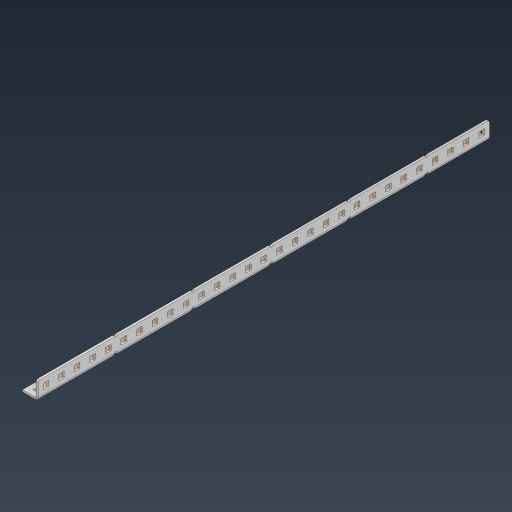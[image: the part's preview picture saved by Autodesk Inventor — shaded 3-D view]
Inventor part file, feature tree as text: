
AUTODESK INVENTOR PART (.ipt)
format: ipt  version: 2024.3 (Build 283343000, 343)  size: 1,099,264 bytes
history: native  units: in
note: dims shown in document units (in); Inventor stores cm internally (conversion verified against a paired STEP export)
features: other x94, extrude x85, sheet_metal_op x11, pattern_linear x2, mirror x1, chamfer x1, sketch x1
ambient origin geometry x8: Origin, YZ Plane, XZ Plane, XY Plane, X Axis, Y Axis, Z Axis, Center Point
bodies: Solid1 (feature_tree), Body (feature_tree)
feature tree (195):
  sheet_metal_op  "Flanges"
  other  "Flange Pattern Plane"
  other  "Flange Pattern Sketch"
  sheet_metal_op  "Flange Pattern"
  sheet_metal_op  "Body Pattern"
  pattern_linear  "Center Pattern"  Spacing1=14.5in  [1 undecoded]
  other  "Arc Length"
  mirror  "Notch Mirror"
  pattern_linear  "Notch Pattern"  Spacing1=0.0625in  [1 undecoded]
  chamfer  "End Chamfer"
  extrude  "Half Cut"  Depth=0.0625in
  other  "Plate1"
  sketch  "Sketch2"  dims[d0=1.0in d1=14.5in d2=0.0625in d3=0.0625in d4=0.0312in d5=0.125in d6=0.0625in d7=0.5in d8=90.0deg d9=0.0312in d10=0.25in d11=0.0625in d12=0.0625in d16=0.182in d17=0.02in d18=0.0625in d19=0.0in d20=0.25in d21=0.25in d38=11.4173in d40=0.5in d41=0.3937in d43=1.0in d46=0.172in d47=1.0in d48=0.0in d49=0.182in d50=0.02in d51=0.25in d52=0.25in d53=0.0625in d54=0.0in d55=0.172in d56=1.0in d57=0.0in d58=0.25in d60=11.4173in d62=0.5in d63=0.3937in d65=0.5in d85=0.1473in d86=0.1782in d88=0.04in d89=0.0625in d90=0.0in d91=0.04in d92=0.0491in d95=2.5in d96=0.04in d97=0.25in d98=45.0deg d99=0.25in d100=0.5in d101=0.0in d102=2.497in d106=0.182in d107=0.02in d108=0.5in d109=0.5in d110=0.0625in d111=0.0in d112=0.172in d113=0.5in d114=0.0in d117=0.5in d118=0.5in d119=0.5in]
  other  "Plate2"
  sheet_metal_op  "Bend1"
  sheet_metal_op  "Corner1"
  other  "Srf1"
  other  "Srf2"
  other  "Srf91"
  sheet_metal_op  "Body Pattern Sketch"
  other  "Srf92"
  other  "Srf786"
  other  "Srf823"
  other  "Srf824"
  other  "Srf825"
  other  "Srf826"
  other  "Srf827"
  other  "Srf828"
  other  "Srf829"
  other  "Srf856"
  other  "Srf857"
  other  "Srf858"
  other  "Srf859"
  other  "Srf860"
  other  "Srf861"
  other  "Srf862"
  other  "Srf889"
  other  "Srf890"
  other  "Srf891"
  other  "Srf892"
  other  "Srf893"
  other  "Srf894"
  other  "Srf895"
  other  "Srf896"
  other  "Srf922"
  other  "Srf923"
  other  "Srf924"
  other  "Srf925"
  other  "Srf926"
  other  "Srf959"
  other  "Srf960"
  other  "Srf961"
  other  "Srf962"
  other  "Srf963"
  other  "Srf996"
  other  "Srf997"
  other  "Srf998"
  other  "Srf999"
  other  "Srf1000"
  other  "Srf1143"
  other  "Srf1144"
  other  "Srf1145"
  other  "Srf1146"
  other  "Srf1147"
  other  "Srf1148"
  other  "Srf1149"
  other  "Srf1150"
  other  "Srf1151"
  other  "Srf1152"
  other  "Srf1153"
  other  "Srf1154"
  other  "Srf1155"
  other  "Srf1156"
  other  "Srf1157"
  other  "Srf1199"
  other  "Srf1200"
  other  "Srf1201"
  other  "Srf1202"
  other  "Srf1203"
  other  "Srf1204"
  other  "Srf1205"
  other  "Srf1206"
  other  "Srf1207"
  other  "Srf1208"
  other  "Srf1209"
  other  "Srf1210"
  other  "Srf1211"
  other  "Srf1212"
  other  "Srf1213"
  other  "Srf1255"
  other  "Srf1256"
  other  "Srf1257"
  other  "Srf1258"
  other  "Srf1259"
  other  "Srf1260"
  other  "Srf1261"
  other  "Srf1262"
  other  "Srf1263"
  other  "Srf1264"
  other  "Srf1265"
  other  "Srf1266"
  other  "Srf1267"
  other  "Srf1268"
  other  "Srf1269"
  sheet_metal_op  "Flange Stamp"
  sheet_metal_op  "Flange Circle"
  sheet_metal_op  "Body Stamp"
  sheet_metal_op  "Body Circle"
  other  "Center Stamp"
  other  "Center Circle"
  sheet_metal_op  "Notch"
  extrude  "ExtrusionSrf2"  Depth=0.0312in
  extrude  "ExtrusionSrf92"  Depth=0.5in
  extrude  "ExtrusionSrf823"  Depth=0.0625in
  extrude  "ExtrusionSrf824"  Depth=0.5in TaperAngle=90.0deg
  extrude  "ExtrusionSrf825"  Depth=0.5in
  extrude  "ExtrusionSrf826"  Depth=0.0625in
  extrude  "ExtrusionSrf827"  Depth=0.0625in
  extrude  "ExtrusionSrf828"  Depth=0.182in
  extrude  "ExtrusionSrf829"  Depth=0.02in
  extrude  "ExtrusionSrf856"  Depth=0.0625in
  extrude  "ExtrusionSrf857"  TaperAngle=0.0deg  [1 undecoded]
  extrude  "ExtrusionSrf858"  Depth=0.5in
  extrude  "ExtrusionSrf859"  Depth=0.5in
  extrude  "ExtrusionSrf860"  Depth=0.5in
  extrude  "ExtrusionSrf861"  Depth=0.5in
  extrude  "ExtrusionSrf862"  Depth=1.0in TaperAngle=0.0deg
  extrude  "ExtrusionSrf889"  Depth=0.182in
  extrude  "ExtrusionSrf890"  Depth=0.02in
  extrude  "ExtrusionSrf891"  Depth=0.5in
  extrude  "ExtrusionSrf892"  Depth=0.5in
  extrude  "ExtrusionSrf893"  Depth=0.0625in
  extrude  "ExtrusionSrf894"  TaperAngle=0.0deg  [1 undecoded]
  extrude  "ExtrusionSrf895"  Depth=0.5in
  extrude  "ExtrusionSrf896"  Depth=1.0in TaperAngle=0.0deg
  extrude  "ExtrusionSrf922"  Depth=0.5in
  extrude  "ExtrusionSrf923"  Depth=0.5in
  extrude  "ExtrusionSrf924"  Depth=0.5in
  extrude  "ExtrusionSrf925"  Depth=0.5in
  extrude  "ExtrusionSrf926"  Depth=0.5in
  extrude  "ExtrusionSrf959"  Depth=0.5in
  extrude  "ExtrusionSrf960"  Depth=0.0625in
  extrude  "ExtrusionSrf961"  TaperAngle=0.0deg  [1 undecoded]
  extrude  "ExtrusionSrf962"  Depth=0.5in
  extrude  "ExtrusionSrf963"  Depth=0.5in
  extrude  "ExtrusionSrf996"  Depth=0.5in
  extrude  "ExtrusionSrf997"  Depth=0.5in TaperAngle=45.0deg
  extrude  "ExtrusionSrf998"  Depth=0.5in
  extrude  "ExtrusionSrf999"  Depth=0.5in TaperAngle=0.0deg
  extrude  "ExtrusionSrf1000"  Depth=0.5in
  extrude  "ExtrusionSrf1143"  Depth=0.182in
  extrude  "ExtrusionSrf1144"  Depth=0.02in
  extrude  "ExtrusionSrf1145"  Depth=0.5in
  extrude  "ExtrusionSrf1146"  Depth=0.5in
  extrude  "ExtrusionSrf1147"  Depth=0.0625in
  extrude  "ExtrusionSrf1148"  TaperAngle=0.0deg  [1 undecoded]
  extrude  "ExtrusionSrf1149"  Depth=0.5in
  extrude  "ExtrusionSrf1150"  Depth=0.5in TaperAngle=0.0deg
  extrude  "ExtrusionSrf1151"  Depth=0.5in
  extrude  "ExtrusionSrf1152"  Depth=0.5in
  extrude  "ExtrusionSrf1153"  Depth=0.5in
  extrude  "ExtrusionSrf1154"  [1 undecoded]
  extrude  "ExtrusionSrf1155"  [1 undecoded]
  extrude  "ExtrusionSrf1156"  [1 undecoded]
  extrude  "ExtrusionSrf1157"  [1 undecoded]
  extrude  "ExtrusionSrf1199"  [1 undecoded]
  extrude  "ExtrusionSrf1200"  [1 undecoded]
  extrude  "ExtrusionSrf1201"  [1 undecoded]
  extrude  "ExtrusionSrf1202"  [1 undecoded]
  extrude  "ExtrusionSrf1203"  [1 undecoded]
  extrude  "ExtrusionSrf1204"  [1 undecoded]
  extrude  "ExtrusionSrf1205"  [1 undecoded]
  extrude  "ExtrusionSrf1206"  [1 undecoded]
  extrude  "ExtrusionSrf1207"  [1 undecoded]
  extrude  "ExtrusionSrf1208"  [1 undecoded]
  extrude  "ExtrusionSrf1209"  [1 undecoded]
  extrude  "ExtrusionSrf1210"  [1 undecoded]
  extrude  "ExtrusionSrf1211"  [1 undecoded]
  extrude  "ExtrusionSrf1212"  [1 undecoded]
  extrude  "ExtrusionSrf1213"  [1 undecoded]
  extrude  "ExtrusionSrf1255"  [1 undecoded]
  extrude  "ExtrusionSrf1256"  [1 undecoded]
  extrude  "ExtrusionSrf1257"  [1 undecoded]
  extrude  "ExtrusionSrf1258"  [1 undecoded]
  extrude  "ExtrusionSrf1259"  [1 undecoded]
  extrude  "ExtrusionSrf1260"  [1 undecoded]
  extrude  "ExtrusionSrf1261"  [1 undecoded]
  extrude  "ExtrusionSrf1262"  [1 undecoded]
  extrude  "ExtrusionSrf1263"  [1 undecoded]
  extrude  "ExtrusionSrf1264"  [1 undecoded]
  extrude  "ExtrusionSrf1265"  [1 undecoded]
  extrude  "ExtrusionSrf1266"  [1 undecoded]
  extrude  "ExtrusionSrf1267"  [1 undecoded]
  extrude  "ExtrusionSrf1268"  [1 undecoded]
  extrude  "ExtrusionSrf1269"  [1 undecoded]
note: 40 required parameter values undecoded (feature->parameter linkage not recoverable at this tier; creation-order binding heuristic only, values carry confidence <= 0.55)
